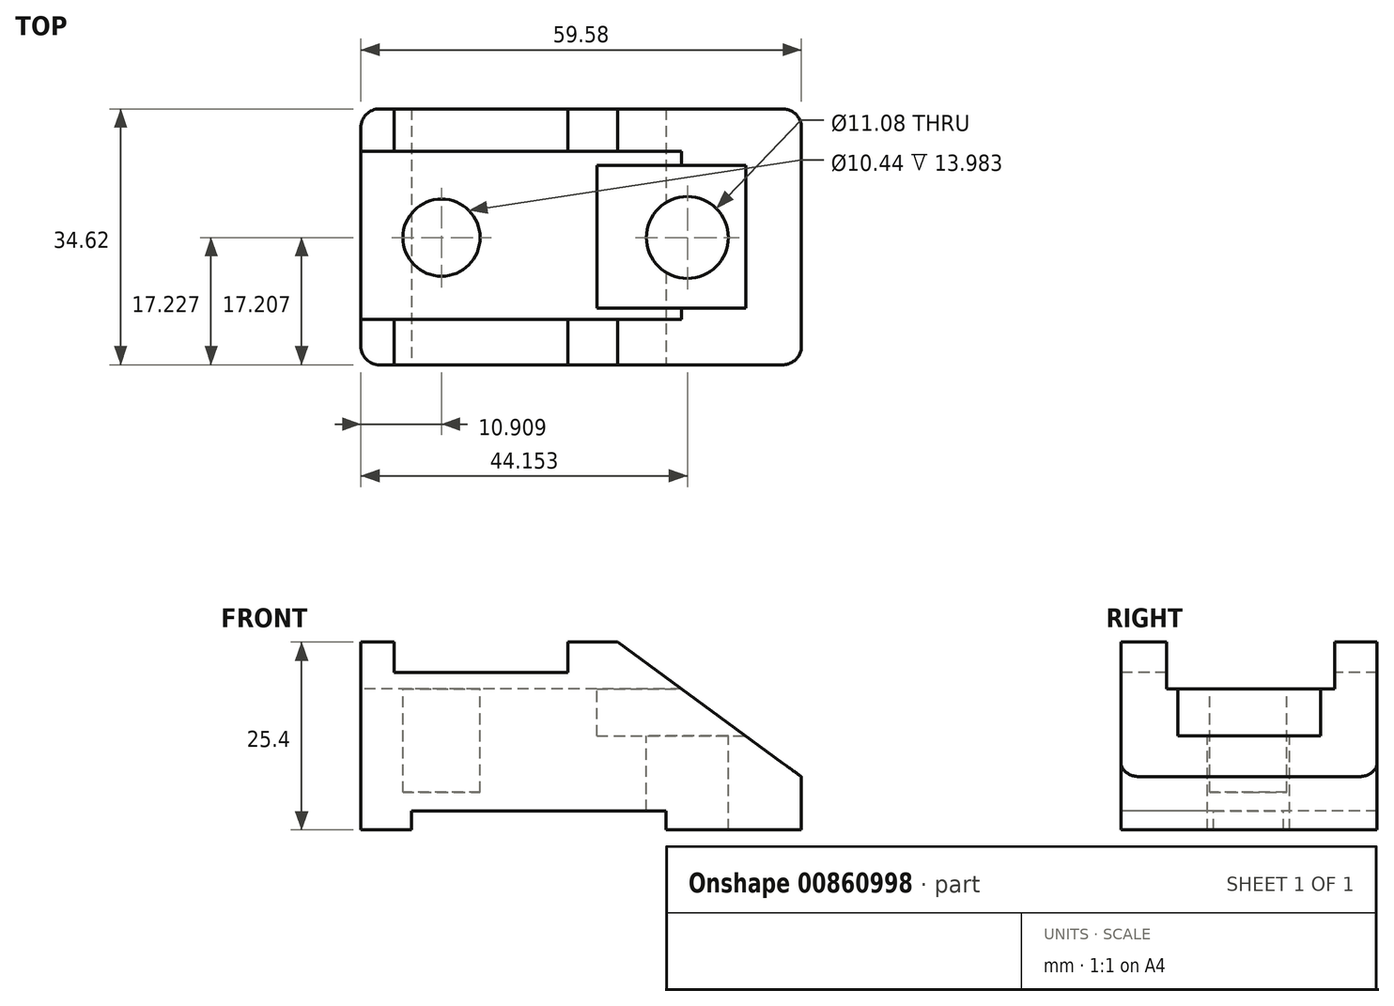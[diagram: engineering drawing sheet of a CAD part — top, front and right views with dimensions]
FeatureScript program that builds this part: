
annotation { "Feature Type Name" : "Feature", "Feature Type Description" : "" }
export const myFeature = defineFeature(function(context is Context, id is Id, definition is map)
    precondition{}
    {
        {
            var Q0;
            Q0=qCreatedBy(makeId("Top.planeOp"),FACE);
            var sketch = newSketch(context, id + "F0", { "sketchPlane" : qUnion([Q0])});
            skLineSegment(sketch, "E0.bottom", {"start": v(0, 0) * mm, "end": v(59.58, 0) * mm});
            skLineSegment(sketch, "E0.top", {"start": v(0, 34.62) * mm, "end": v(59.58, 34.62) * mm});
            skLineSegment(sketch, "E0.left", {"start": v(0, 0) * mm, "end": v(0, 34.62) * mm});
            skLineSegment(sketch, "E0.right", {"start": v(59.58, 0) * mm, "end": v(59.58, 34.62) * mm});
            skSolve(sketch);
        }
        {
            var Q0;
            Q0=makeQuery(id+"F0.imprint","IMPRINT",FACE,{"disambiguationData":[TD([[makeQuery(id+"F0.imprint","IMPRINT",EDGE,{"derivedFrom":sQuery(id+"F0.wireOp",EDGE,"E0.bottom")}),1.0]])]});
            extrude(context, id + "F1", {"entities" : qUnion([Q0]), "depth" : 25.4 * mm, "offsetDistance" : 25.4 * mm});
        }
        {
            var Q0;
            Q0=makeQuery(id+"F1.opExtrude","CAP_FACE",FACE,{"disambiguationData":[OSD([sQuery(id+"F0.wireOp",EDGE,"E0.bottom"),sQuery(id+"F0.wireOp",EDGE,"E0.top"),sQuery(id+"F0.wireOp",EDGE,"E0.left"),sQuery(id+"F0.wireOp",EDGE,"E0.right")])],"isStart":false});
            var sketch = newSketch(context, id + "F2", { "sketchPlane" : qUnion([Q0])});
            skCircle(sketch, "E1", {"center": v(10.9, 17.2) * mm, "radius": 5.22 * mm});
            skCircle(sketch, "E2", {"center": v(43.45, 17.62) * mm, "radius": 8.71 * mm});
            skSolve(sketch);
        }
        {
            var Q0;
            Q0=makeQuery(id+"F1.opExtrude","CAP_FACE",FACE,{"disambiguationData":[OSD([sQuery(id+"F0.wireOp",EDGE,"E0.bottom"),sQuery(id+"F0.wireOp",EDGE,"E0.top"),sQuery(id+"F0.wireOp",EDGE,"E0.left"),sQuery(id+"F0.wireOp",EDGE,"E0.right")])],"isStart":false});
            var sketch = newSketch(context, id + "F3", { "sketchPlane" : qUnion([Q0])});
            skCircle(sketch, "E3", {"center": v(44.15, 17.23) * mm, "radius": 5.54 * mm});
            skSolve(sketch);
        }
        {
            var Q0;
            Q0=makeQuery(id+"F3.imprint","IMPRINT",FACE,{"disambiguationData":[TD([[makeQuery(id+"F3.imprint","IMPRINT",EDGE,{"derivedFrom":sQuery(id+"F3.wireOp",EDGE,"E3")}),1.0]])]});
            extrude(context, id + "F4", {"entities" : qUnion([Q0]), "operationType" : NewBodyOperationType.REMOVE, "endBound" : BoundingType.THROUGH_ALL, "oppositeDirection" : true, "depth" : 25.4 * mm, "offsetDistance" : 25.4 * mm});
        }
        {
            var Q0;
            Q0=makeQuery(id+"F1.opExtrude","CAP_FACE",FACE,{"disambiguationData":[OSD([sQuery(id+"F0.wireOp",EDGE,"E0.bottom"),sQuery(id+"F0.wireOp",EDGE,"E0.top"),sQuery(id+"F0.wireOp",EDGE,"E0.left"),sQuery(id+"F0.wireOp",EDGE,"E0.right")])],"isStart":false});
            var sketch = newSketch(context, id + "F5", { "sketchPlane" : qUnion([Q0])});
            skLineSegment(sketch, "E4.bottom", {"start": v(31.91, 26.99) * mm, "end": v(59.58, 26.99) * mm});
            skLineSegment(sketch, "E4.top", {"start": v(31.91, 7.7) * mm, "end": v(59.58, 7.7) * mm});
            skLineSegment(sketch, "E4.left", {"start": v(31.91, 26.99) * mm, "end": v(31.91, 7.7) * mm});
            skLineSegment(sketch, "E4.right", {"start": v(59.58, 26.99) * mm, "end": v(59.58, 7.7) * mm});
            skSolve(sketch);
        }
        {
            var Q0;
            Q0=makeQuery(id+"F5.imprint","IMPRINT",FACE,{"disambiguationData":[TD([[makeQuery(id+"F5.imprint","IMPRINT",EDGE,{"derivedFrom":sQuery(id+"F5.wireOp",EDGE,"E4.bottom")}),-1.0]])]});
            extrude(context, id + "F6", {"entities" : qUnion([Q0]), "operationType" : NewBodyOperationType.REMOVE, "oppositeDirection" : true, "depth" : 12.7 * mm, "offsetDistance" : 25.4 * mm});
        }
        {
            var Q0;
            Q0=makeQuery(id+"F1.opExtrude","SWEPT_FACE",FACE,{"disambiguationData":[OSD([sQuery(id+"F0.wireOp",EDGE,"E0.bottom")])]});
            var sketch = newSketch(context, id + "F7", { "sketchPlane" : qUnion([Q0])});
            skLineSegment(sketch, "E5", {"start": v(34.72, 25.4) * mm, "end": v(59.58, 7.2) * mm});
            skSolve(sketch);
        }
        {
            var Q0;
            {var subQ0=sQuery(id+"F7.wireOp",EDGE,"E5");Q0=makeQuery(id+"F7.imprint","IMPRINT",FACE,{"disambiguationData":[TD([[makeQuery(id+"F7.imprint","IMPRINT",EDGE,{"derivedFrom":subQ0}),1.0]])]});}
            extrude(context, id + "F8", {"entities" : qUnion([Q0]), "operationType" : NewBodyOperationType.REMOVE, "endBound" : BoundingType.THROUGH_ALL, "oppositeDirection" : true, "depth" : 25.4 * mm, "offsetDistance" : 25.4 * mm});
        }
        {
            var Q0;
            Q0=makeQuery(id+"F1.opExtrude","SWEPT_FACE",FACE,{"disambiguationData":[OSD([sQuery(id+"F0.wireOp",EDGE,"E0.bottom")])]});
            var sketch = newSketch(context, id + "F9", { "sketchPlane" : qUnion([Q0])});
            skLineSegment(sketch, "E6.bottom", {"start": v(6.86, 0) * mm, "end": v(41.28, 0) * mm});
            skLineSegment(sketch, "E6.top", {"start": v(6.86, 2.58) * mm, "end": v(41.28, 2.58) * mm});
            skLineSegment(sketch, "E6.left", {"start": v(6.86, 0) * mm, "end": v(6.86, 2.58) * mm});
            skLineSegment(sketch, "E6.right", {"start": v(41.28, 0) * mm, "end": v(41.28, 2.58) * mm});
            skLineSegment(sketch, "E7.bottom", {"start": v(4.51, 25.4) * mm, "end": v(28.02, 25.4) * mm});
            skLineSegment(sketch, "E7.top", {"start": v(4.51, 21.27) * mm, "end": v(28.02, 21.27) * mm});
            skLineSegment(sketch, "E7.left", {"start": v(4.51, 25.4) * mm, "end": v(4.51, 21.27) * mm});
            skLineSegment(sketch, "E7.right", {"start": v(28.02, 25.4) * mm, "end": v(28.02, 21.27) * mm});
            skLineSegment(sketch, "E8.bottom", {"start": v(8.5, 21.27) * mm, "end": v(24.6, 21.27) * mm});
            skLineSegment(sketch, "E8.top", {"start": v(8.5, 18.2) * mm, "end": v(24.6, 18.2) * mm});
            skLineSegment(sketch, "E8.left", {"start": v(8.5, 21.27) * mm, "end": v(8.5, 18.2) * mm});
            skLineSegment(sketch, "E8.right", {"start": v(24.6, 21.27) * mm, "end": v(24.6, 18.2) * mm});
            skSolve(sketch);
        }
        {
            var Q0;
            Q0=makeQuery(id+"F9.imprint","IMPRINT",FACE,{"disambiguationData":[TD([[makeQuery(id+"F9.imprint","IMPRINT",EDGE,{"derivedFrom":sQuery(id+"F9.wireOp",EDGE,"E7.bottom")}),-1.0]])]});
            var Q1;
            Q1=makeQuery(id+"F9.imprint","IMPRINT",FACE,{"disambiguationData":[TD([[makeQuery(id+"F9.imprint","IMPRINT",EDGE,{"derivedFrom":sQuery(id+"F9.wireOp",EDGE,"E8.bottom")}),-1.0]])]});
            var Q2;
            Q2=makeQuery(id+"F9.imprint","IMPRINT",FACE,{"disambiguationData":[TD([[makeQuery(id+"F9.imprint","IMPRINT",EDGE,{"derivedFrom":sQuery(id+"F9.wireOp",EDGE,"E6.bottom")}),1.0]])]});
            extrude(context, id + "F10", {"entities" : qUnion([Q0, Q1, Q2]), "operationType" : NewBodyOperationType.REMOVE, "endBound" : BoundingType.THROUGH_ALL, "oppositeDirection" : true, "depth" : 25.4 * mm, "offsetDistance" : 25.4 * mm});
        }
        {
            var Q0;
            Q0=makeQuery(id+"F1.opExtrude","SWEPT_FACE",FACE,{"disambiguationData":[OSD([sQuery(id+"F0.wireOp",EDGE,"E0.left")])]});
            var sketch = newSketch(context, id + "F11", { "sketchPlane" : qUnion([Q0])});
            skLineSegment(sketch, "E9.bottom", {"start": v(-28.89, 25.4) * mm, "end": v(-6.15, 25.4) * mm});
            skLineSegment(sketch, "E9.top", {"start": v(-28.89, 19.06) * mm, "end": v(-6.15, 19.06) * mm});
            skLineSegment(sketch, "E9.left", {"start": v(-28.89, 25.4) * mm, "end": v(-28.89, 19.06) * mm});
            skLineSegment(sketch, "E9.right", {"start": v(-6.15, 25.4) * mm, "end": v(-6.15, 19.06) * mm});
            skLineSegment(sketch, "E10.bottom", {"start": v(-24.3, 19.06) * mm, "end": v(-10.95, 19.06) * mm});
            skLineSegment(sketch, "E10.top", {"start": v(-24.3, 13.01) * mm, "end": v(-10.95, 13.01) * mm});
            skLineSegment(sketch, "E10.left", {"start": v(-24.3, 19.06) * mm, "end": v(-24.3, 13.01) * mm});
            skLineSegment(sketch, "E10.right", {"start": v(-10.95, 19.06) * mm, "end": v(-10.95, 13.01) * mm});
            skSolve(sketch);
        }
        {
            var Q0;
            Q0=makeQuery(id+"F11.imprint","IMPRINT",FACE,{"disambiguationData":[TD([[makeQuery(id+"F11.imprint","IMPRINT",EDGE,{"derivedFrom":sQuery(id+"F11.wireOp",EDGE,"E9.bottom")}),1.0]])]});
            var Q1;
            Q1=makeQuery(id+"F11.imprint","IMPRINT",FACE,{"disambiguationData":[TD([[makeQuery(id+"F11.imprint","IMPRINT",EDGE,{"derivedFrom":sQuery(id+"F11.wireOp",EDGE,"E10.bottom")}),-1.0]])]});
            extrude(context, id + "F12", {"entities" : qUnion([Q0, Q1]), "operationType" : NewBodyOperationType.REMOVE, "endBound" : BoundingType.THROUGH_ALL, "oppositeDirection" : true, "depth" : 25.4 * mm, "offsetDistance" : 25.4 * mm});
        }
        {
            var Q0;
            Q0=makeQuery(id+"F2.imprint","IMPRINT",FACE,{"disambiguationData":[TD([[makeQuery(id+"F2.imprint","IMPRINT",EDGE,{"derivedFrom":sQuery(id+"F2.wireOp",EDGE,"E1")}),-1.0]])]});
            var sketch = newSketch(context, id + "F13", { "sketchPlane" : qUnion([Q0])});
            skSolve(sketch);
        }
        {
            var Q0;
            Q0=makeQuery(id+"F2.imprint","IMPRINT",FACE,{"disambiguationData":[TD([[makeQuery(id+"F2.imprint","IMPRINT",EDGE,{"derivedFrom":sQuery(id+"F2.wireOp",EDGE,"E1")}),1.0]])]});
            extrude(context, id + "F14", {"entities" : qUnion([Q0]), "operationType" : NewBodyOperationType.REMOVE, "oppositeDirection" : true, "depth" : 7.62 * mm, "offsetDistance" : 25.4 * mm});
        }
        {
            var Q0;
            Q0=makeQuery(id+"F13.imprint","IMPRINT",FACE,{"disambiguationData":[TD([[makeQuery(id+"F13.imprint","IMPRINT",EDGE,{"derivedFrom":makeQuery(id+"F2.imprint","IMPRINT",EDGE,{"derivedFrom":sQuery(id+"F2.wireOp",EDGE,"E1")})}),1.0]])]});
            extrude(context, id + "F15", {"entities" : qUnion([Q0]), "operationType" : NewBodyOperationType.REMOVE, "oppositeDirection" : true, "depth" : 20.32 * mm, "offsetDistance" : 25.4 * mm});
        }
        {
            var Q0;
            Q0=makeQuery(id+"F1.opExtrude","SWEPT_EDGE",EDGE,{"disambiguationData":[OSD([sQuery(id+"F0.wireOp",EDGE,"E0.bottom"),sQuery(id+"F0.wireOp",EDGE,"E0.left")])]});
            var Q1;
            Q1=makeQuery(id+"F1.opExtrude","SWEPT_EDGE",EDGE,{"disambiguationData":[OSD([sQuery(id+"F0.wireOp",EDGE,"E0.bottom"),sQuery(id+"F0.wireOp",EDGE,"E0.right")])]});
            var Q2;
            Q2=makeQuery(id+"F1.opExtrude","SWEPT_EDGE",EDGE,{"disambiguationData":[OSD([sQuery(id+"F0.wireOp",EDGE,"E0.top"),sQuery(id+"F0.wireOp",EDGE,"E0.right")])]});
            var Q3;
            Q3=makeQuery(id+"F1.opExtrude","SWEPT_EDGE",EDGE,{"disambiguationData":[OSD([sQuery(id+"F0.wireOp",EDGE,"E0.top"),sQuery(id+"F0.wireOp",EDGE,"E0.left")])]});
            fillet(context, id + "F16", {"entities" : qUnion([Q0, Q1, Q2, Q3]), "radius" : 2.54 * mm, "tangentPropagation" : true, "allowEdgeOverflow" : false});
        }
    });
